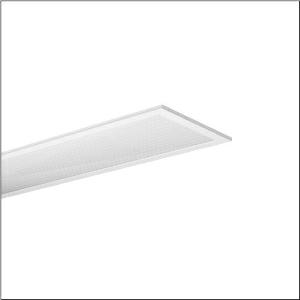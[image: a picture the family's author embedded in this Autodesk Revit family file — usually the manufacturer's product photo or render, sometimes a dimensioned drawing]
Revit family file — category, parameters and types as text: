
# Revit family: apollon_r__21_linear_51mq17wd2312_219c
name_source: partatom
category: Lighting Fixtures
units: mm (PartAtom-declared; Revit-internal decimal feet)

## family parameters
Cut with Voids When Loaded = No
Host = Face
Light Source = No
Part Type = Normal
Room Calculation Point = No
Round Connector Dimension = Use Diameter
Shared = No

## types (1)
- Apollon® 21 linear (1 x LED, 6900 lm, 60 W, 3000K)
    Apparent Load = 60 VA
    CIE Flux Codes = 61 87 97 100 100
    Color Rendering = 80
    Color Temperature = 3000K
    Default Elevation = 1800 mm
    Description = Apollon® 21 linear, office luminaire, primary optical cover: micro prismatic cover, CAT 2 (L<= 3000cd/m²), light emission: direct distribution, primary light characteristic: symmetric, installation type: lay-in mounting, LED, rated luminous flux: 6.900lm, luminous efficacy: 115lm/W, light colour: 830, colour temperature: 3000K, with terminal, 5-pole, mains connection: 220..240V, AC, 50/60Hz, rated input power: 60W, housing, of aluminium, coated, pure white, length: 1.545mm, width: 307mm, height: 39mm, housing upper side, of sheet steel, galvanised, protection rating (complete): IP20, protection rating (lamp compartment, on room side): IP50, insulation class (complete): insulation class II (safety insulation), certification: CE, ENEC, packaging unit: 1 piece
    Height = 0 mm  [stored 0 ft]
    Lamp = 1 x LED
    Lamp Light Flux = 6900 lm
    Lamp Power = 60 W
    Lamp count = 1
    Length = 1545 mm
    Luminous efficacy = 115 lm/W
    Manufacturer = Siteco
    ModVariant = No
    Model = 51MQ17WD2312
    Mounting Place = Ceiling
    Mounting Type = Recessed
    Number of Poles = 1
    OnlyDefault = Yes
    Power Factor = 1
    Product Name = Apollon® 21 linear
    Product group = office luminaire | ceiling recessed
    ProductGroupID = 401
    Protection Class = Protection class II
    Protection Degree = IP 20
    RLX_Detail_Level = 1
    RLX_Emergency_Light_Flux = 0 lm
    RLX_Emergency_Type = 0
    RLX_Emergency_Type_DB = No
    RlxData = <blob elided: 17205 chars, md5=1d77698e>
    Socket = socket
    Standby Power = 0 W
    System Light Flux = 6900 lm
    System Power = 60 W
    Type Comments = Product without accessories
    Type Image = l_1291045.jpg
    URL = http://relux.com
    VarID = ---
    Voltage = 0 V
    Weight = 0.00 kg
    Width = 307 mm

note: [stored X ft] marks values corroborated as IEEE doubles in the binary element streams (Revit-internal decimal feet)

## geometry (parser evidence)
native form markers: Blend x4, Sweep x9
no freeform markers — native parametric forms only
